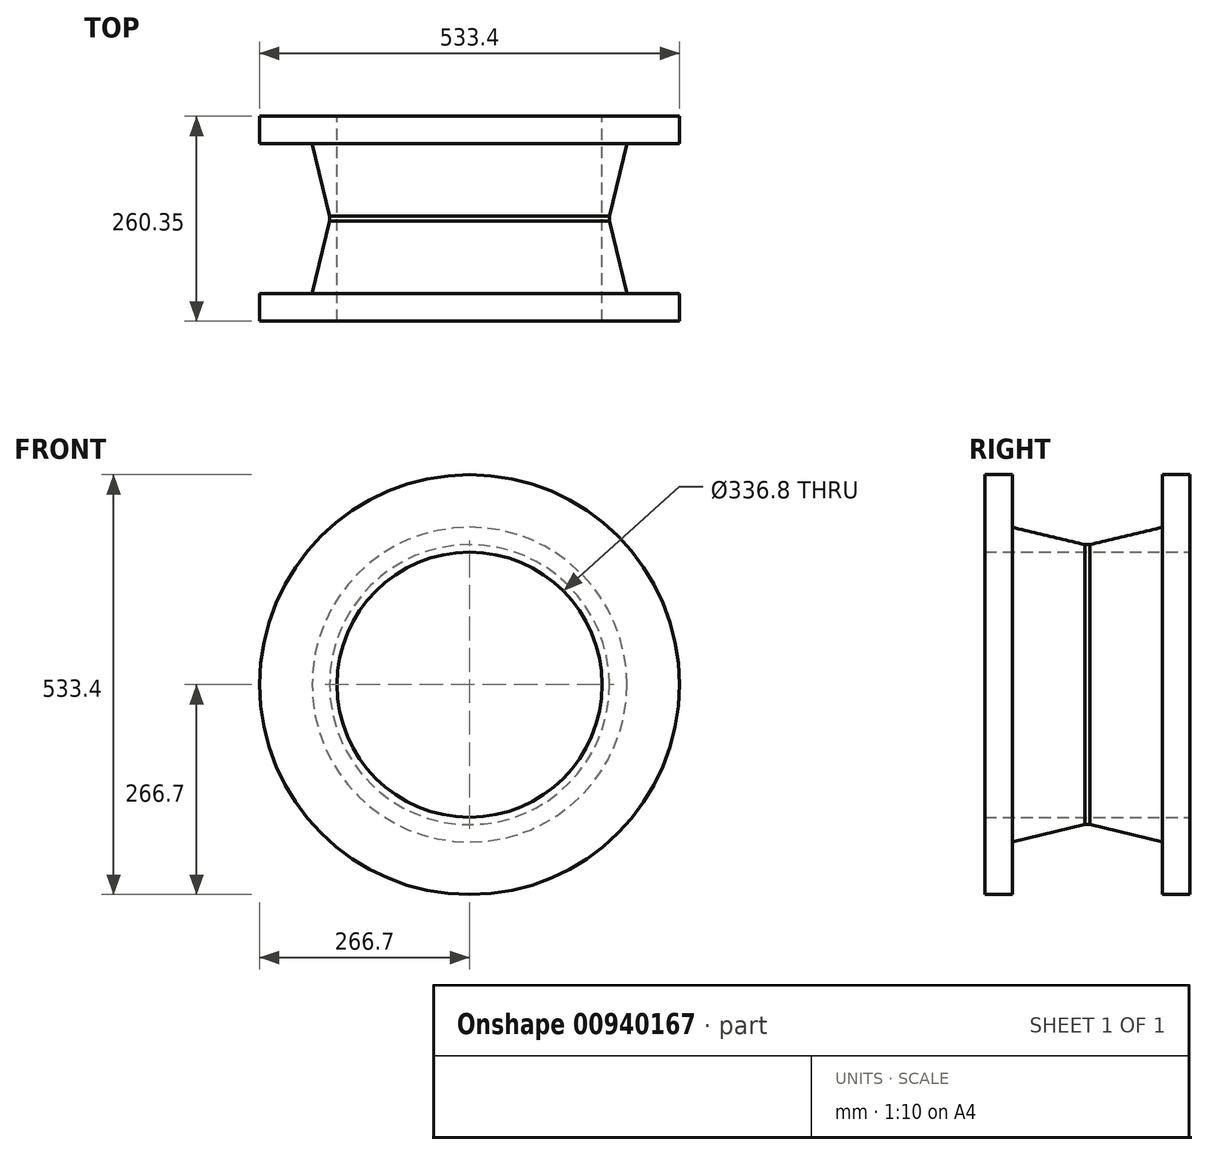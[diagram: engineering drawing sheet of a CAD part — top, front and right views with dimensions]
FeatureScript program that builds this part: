
annotation { "Feature Type Name" : "Feature", "Feature Type Description" : "" }
export const myFeature = defineFeature(function(context is Context, id is Id, definition is map)
    precondition{}
    {
        {
            var Q0;
            Q0=qCreatedBy(makeId("Top.planeOp"),FACE);
            var sketch = newSketch(context, id + "F0", { "sketchPlane" : qUnion([Q0])});
            skLineSegment(sketch, "E0", {"start": v(0, 0) * mm, "end": v(266.7, 0) * mm, "construction": true});
            skLineSegment(sketch, "E1", {"start": v(266.7, 0) * mm, "end": v(266.7, 34.93) * mm});
            skLineSegment(sketch, "E2", {"start": v(266.7, 34.93) * mm, "end": v(200.03, 34.93) * mm});
            skLineSegment(sketch, "E3", {"start": v(200.03, 34.92) * mm, "end": v(177.8, 127) * mm});
            skLineSegment(sketch, "E4", {"start": v(177.8, 127) * mm, "end": v(168.4, 127) * mm});
            skLineSegment(sketch, "E5", {"start": v(168.4, 127) * mm, "end": v(168.4, 0) * mm});
            skLineSegment(sketch, "E6", {"start": v(168.4, 0) * mm, "end": v(266.7, 0) * mm});
            skLineSegment(sketch, "E7", {"start": v(0, 127) * mm, "end": v(0, 0) * mm, "construction": true});
            skSolve(sketch);
        }
        {
            var Q0;
            Q0=qSketchRegion(id+"F0",true);
            var Q1;
            Q1=sQuery(id+"F0.wireOp",EDGE,"E7");
            revolve(context, id + "F1", {"entities" : qUnion([Q0]), "axis" : qUnion([Q1]), "revolveType" : RevolveType.FULL});
        }
        {
            var Q0;
            Q0=qCreatedBy(makeId("Front.planeOp"),FACE);
            cPlane(context, id + "F2", {"entities" : qUnion([Q0]), "cplaneType" : CPlaneType.OFFSET, "offset" : 130.17 * mm, "oppositeDirection" : true, "width" : 152.4 * mm, "height" : 152.4 * mm});
        }
        {
            var Q0;
            Q0=makeQuery(id+"F1.opRevolve","SWEPT_BODY",BODY,{"disambiguationData":[OSD([sQuery(id+"F0.wireOp",EDGE,"E1"),sQuery(id+"F0.wireOp",EDGE,"E2"),sQuery(id+"F0.wireOp",EDGE,"E3"),sQuery(id+"F0.wireOp",EDGE,"E4"),sQuery(id+"F0.wireOp",EDGE,"E5"),sQuery(id+"F0.wireOp",EDGE,"E6")])]});
            var Q1;
            Q1=qCreatedBy(id+"F2.planeOp",FACE);
            mirror(context, id + "F3", {"entities" : qUnion([Q0]), "mirrorPlane" : qUnion([Q1])});
        }
        {
            var Q0;
            Q0=qCreatedBy(makeId("Top.planeOp"),FACE);
            var sketch = newSketch(context, id + "F4", { "sketchPlane" : qUnion([Q0])});
            skLineSegment(sketch, "E8.bottom", {"start": v(168.4, 127) * mm, "end": v(177.8, 127) * mm});
            skLineSegment(sketch, "E8.top", {"start": v(168.4, 133.35) * mm, "end": v(177.8, 133.35) * mm});
            skLineSegment(sketch, "E8.left", {"start": v(177.8, 133.35) * mm, "end": v(177.8, 127) * mm});
            skLineSegment(sketch, "E8.right", {"start": v(168.4, 133.35) * mm, "end": v(168.4, 127) * mm});
            skSolve(sketch);
        }
        {
            var Q0;
            Q0=qSketchRegion(id+"F4",true);
            var Q1;
            Q1=sQuery(id+"F0.wireOp",EDGE,"E7");
            revolve(context, id + "F5", {"operationType" : NewBodyOperationType.ADD, "entities" : qUnion([Q0]), "axis" : qUnion([Q1]), "revolveType" : RevolveType.FULL});
        }
    });
